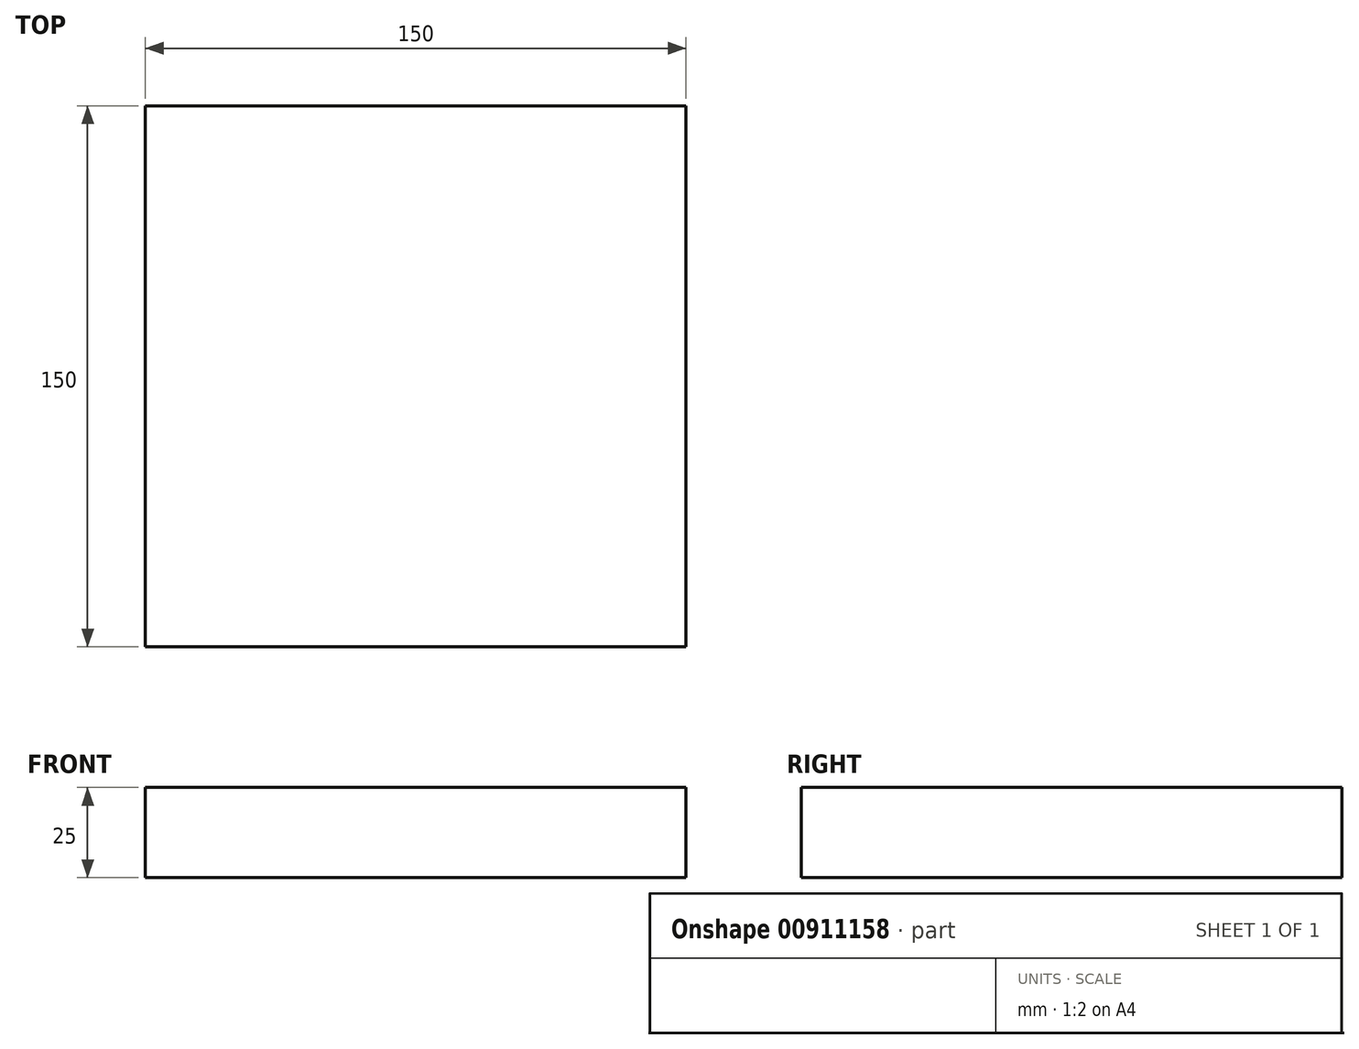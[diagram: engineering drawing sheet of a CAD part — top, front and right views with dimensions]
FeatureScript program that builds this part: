
annotation { "Feature Type Name" : "Feature", "Feature Type Description" : "" }
export const myFeature = defineFeature(function(context is Context, id is Id, definition is map)
    precondition{}
    {
        {
            var Q0;
            Q0=qCreatedBy(makeId("Top.planeOp"),FACE);
            var sketch = newSketch(context, id + "F0", { "sketchPlane" : qUnion([Q0])});
            skLineSegment(sketch, "E0.bottom", {"start": v(-60.89, 83.38) * mm, "end": v(89.11, 83.38) * mm});
            skLineSegment(sketch, "E0.top", {"start": v(-60.89, -66.62) * mm, "end": v(89.11, -66.62) * mm});
            skLineSegment(sketch, "E0.left", {"start": v(-60.89, 83.38) * mm, "end": v(-60.89, -66.62) * mm});
            skLineSegment(sketch, "E0.right", {"start": v(89.11, 83.38) * mm, "end": v(89.11, -66.62) * mm});
            skSolve(sketch);
        }
        {
            var Q0;
            Q0 = qSketchRegion(id + "F0", true);
            extrude(context, id + "F1", {"entities" : qUnion([Q0]), "depth" : 25 * mm, "offsetDistance" : 25 * mm});
        }
    });
